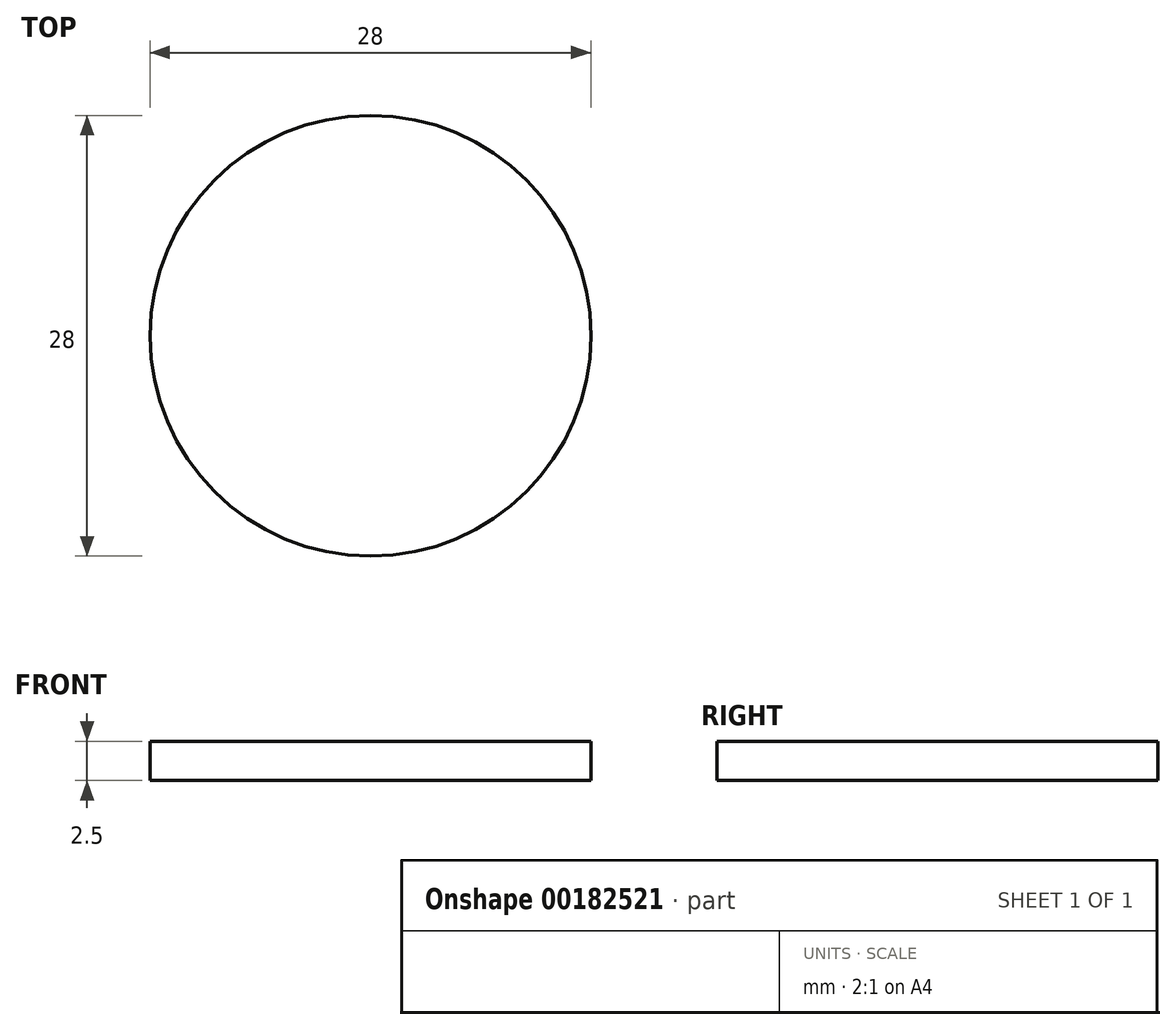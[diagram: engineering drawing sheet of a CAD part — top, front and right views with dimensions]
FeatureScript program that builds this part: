
annotation { "Feature Type Name" : "Feature", "Feature Type Description" : "" }
export const myFeature = defineFeature(function(context is Context, id is Id, definition is map)
    precondition{}
    {
        {
            var Q0;
            Q0=qCreatedBy(makeId("Top.planeOp"),FACE);
            var sketch = newSketch(context, id + "F0", { "sketchPlane" : qUnion([Q0])});
            skCircle(sketch, "E0", {"center": v(0, 0) * mm, "radius": 14 * mm});
            skLineSegment(sketch, "E1", {"start": v(0, 0) * mm, "end": v(7, 12.12) * mm});
            skLineSegment(sketch, "E2", {"start": v(0, 0) * mm, "end": v(14, 0) * mm});
            skSolve(sketch);
        }
        {
            var Q0;
            {var subQ0=sQuery(id+"F0.wireOp",EDGE,"E1");Q0=makeQuery(id+"F0.imprint","IMPRINT",FACE,{"disambiguationData":[TD([[makeQuery(id+"F0.imprint","IMPRINT",EDGE,{"derivedFrom":subQ0}),1.0]])]});}
            var Q1;
            {var subQ0=sQuery(id+"F0.wireOp",EDGE,"E1");Q1=makeQuery(id+"F0.imprint","IMPRINT",FACE,{"disambiguationData":[TD([[makeQuery(id+"F0.imprint","IMPRINT",EDGE,{"derivedFrom":subQ0}),-1.0]])]});}
            extrude(context, id + "F1", {"entities" : qUnion([Q0, Q1]), "depth" : 2.5 * mm});
        }
    });
